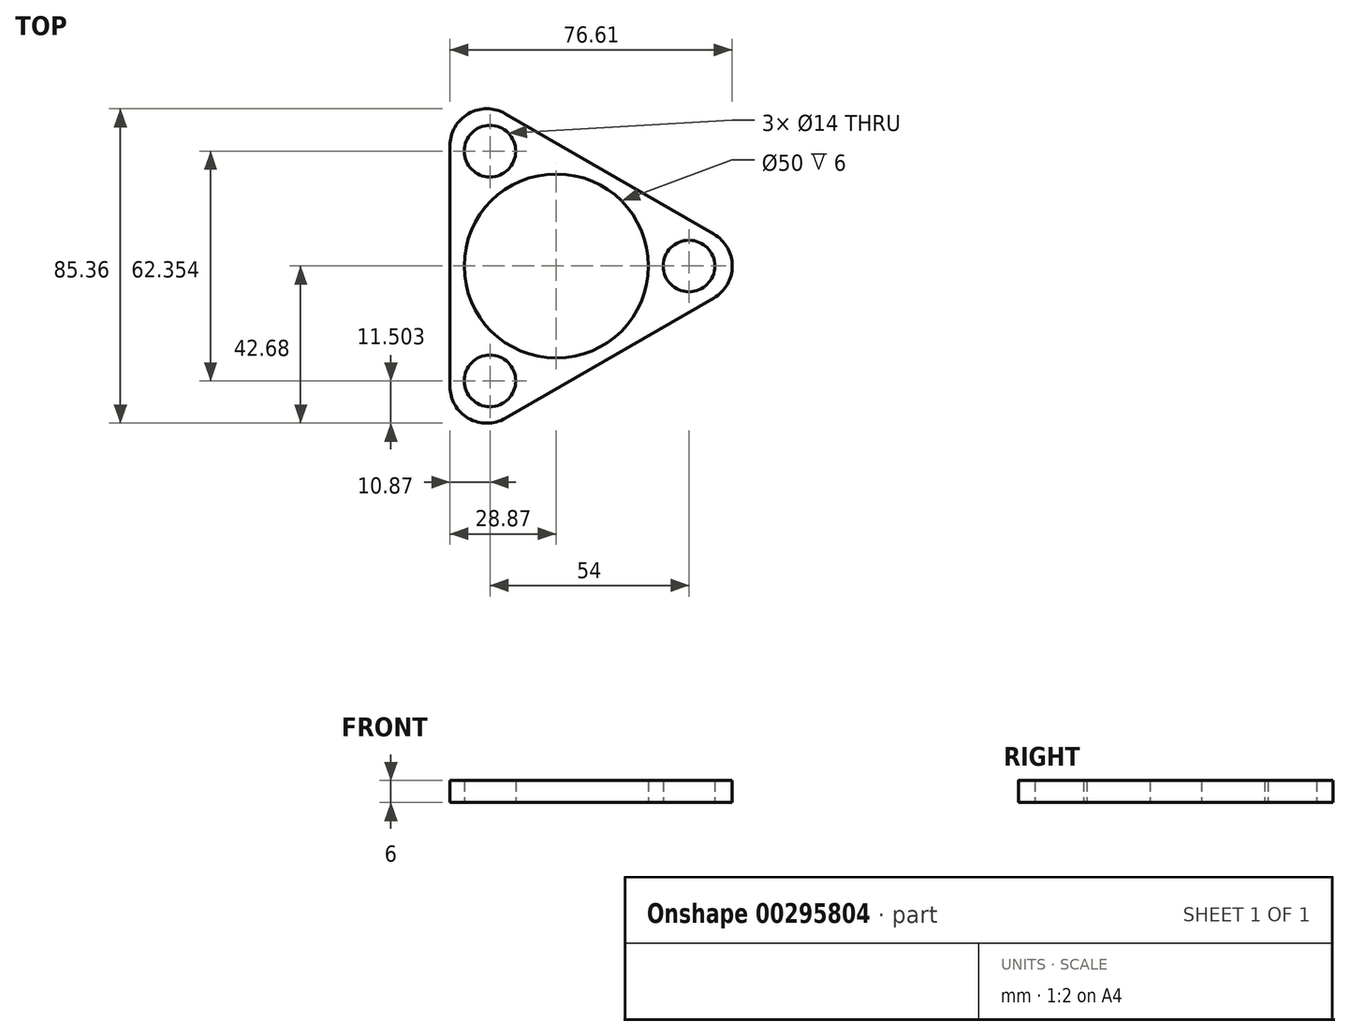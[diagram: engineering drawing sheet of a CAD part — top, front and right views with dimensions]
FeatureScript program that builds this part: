
annotation { "Feature Type Name" : "Feature", "Feature Type Description" : "" }
export const myFeature = defineFeature(function(context is Context, id is Id, definition is map)
    precondition{}
    {
        {
            var Q0;
            Q0=qCreatedBy(makeId("Top.planeOp"),FACE);
            var sketch = newSketch(context, id + "F0", { "sketchPlane" : qUnion([Q0])});
            skCircle(sketch, "E0.cCircle", {"center": v(0, 0) * mm, "radius": 28.87 * mm, "construction": true});
            skLineSegment(sketch, "E0.0", {"start": v(-28.87, -50) * mm, "end": v(-28.87, 50) * mm});
            skLineSegment(sketch, "E0.1", {"start": v(-28.87, 50) * mm, "end": v(57.74, 0) * mm});
            skLineSegment(sketch, "E0.2", {"start": v(57.74, 0) * mm, "end": v(-28.87, -50) * mm});
            skPoint(sketch, "E0.0.midPoint", {"position": v(-28.87, 0) * mm});
            skLineSegment(sketch, "E1", {"start": v(0, 0) * mm, "end": v(57.74, 0) * mm, "construction": true});
            skCircle(sketch, "E2", {"center": v(36, 0) * mm, "radius": 7 * mm});
            skCircle(sketch, "E3.1.0", {"center": v(-18, 31.18) * mm, "radius": 7 * mm});
            skCircle(sketch, "E3.2.0", {"center": v(-18, -31.18) * mm, "radius": 7 * mm});
            skCircle(sketch, "E4", {"center": v(0, 0) * mm, "radius": 25 * mm});
            skSolve(sketch);
        }
        {
            var Q0;
            Q0 = qSketchRegion(id + "F0", true);
            extrude(context, id + "F1", {"entities" : qUnion([Q0]), "depth" : 6 * mm});
        }
        {
            var Q0;
            Q0=makeQuery(id+"F1.opExtrude","SWEPT_EDGE",EDGE,{"disambiguationData":[OSD([sQuery(id+"F0.wireOp",EDGE,"E0.0"),sQuery(id+"F0.wireOp",EDGE,"E0.2")])]});
            var Q1;
            Q1=makeQuery(id+"F1.opExtrude","SWEPT_EDGE",EDGE,{"disambiguationData":[OSD([sQuery(id+"F0.wireOp",EDGE,"E0.1"),sQuery(id+"F0.wireOp",EDGE,"E0.2")])]});
            var Q2;
            Q2=makeQuery(id+"F1.opExtrude","SWEPT_EDGE",EDGE,{"disambiguationData":[OSD([sQuery(id+"F0.wireOp",EDGE,"E0.0"),sQuery(id+"F0.wireOp",EDGE,"E0.1")])]});
            fillet(context, id + "F2", {"entities" : qUnion([Q0, Q1, Q2]), "radius" : 10 * mm, "tangentPropagation" : true, "allowEdgeOverflow" : false});
        }
    });
